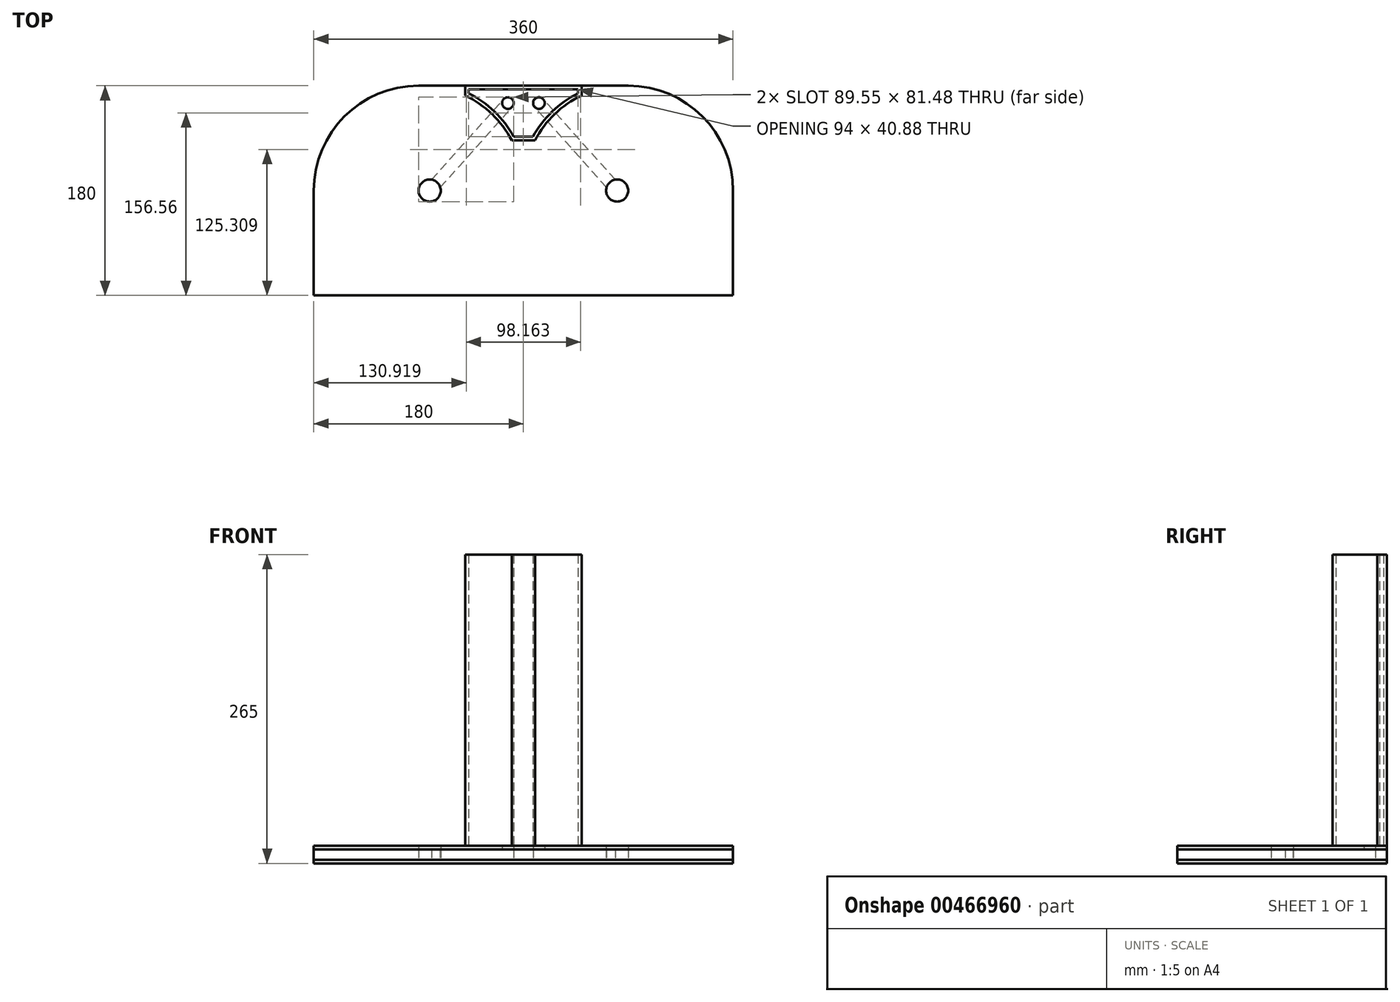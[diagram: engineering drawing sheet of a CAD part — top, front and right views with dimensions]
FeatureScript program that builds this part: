
annotation { "Feature Type Name" : "Feature", "Feature Type Description" : "" }
export const myFeature = defineFeature(function(context is Context, id is Id, definition is map)
    precondition{}
    {
        {
            var Q0;
            Q0=qCreatedBy(makeId("Top.planeOp"),FACE);
            var sketch = newSketch(context, id + "F0", { "sketchPlane" : qUnion([Q0])});
            skLineSegment(sketch, "E0.bottom", {"start": v(-180, 90) * mm, "end": v(180, 90) * mm});
            skLineSegment(sketch, "E0.top", {"start": v(-180, -90) * mm, "end": v(180, -90) * mm});
            skLineSegment(sketch, "E0.left", {"start": v(-180, 90) * mm, "end": v(-180, -90) * mm});
            skLineSegment(sketch, "E0.right", {"start": v(180, 90) * mm, "end": v(180, -90) * mm});
            skPoint(sketch, "E0.middle", {"position": v(0, 0) * mm});
            skArc(sketch, "E1", {"start": v(-78.84, 9.35) * mm, "mid": v(-86.83, -7.08) * mm, "end": v(-71.39, 2.69) * mm});
            skLineSegment(sketch, "E2", {"start": v(-80.5, 0) * mm, "end": v(0, 90) * mm, "construction": true});
            skLineSegment(sketch, "E3.0", {"start": v(-71.39, 2.69) * mm, "end": v(-9.6, 71.76) * mm});
            skLineSegment(sketch, "E4.0", {"start": v(-78.84, 9.35) * mm, "end": v(-17.06, 78.43) * mm});
            skArc(sketch, "E5", {"start": v(-9.6, 71.76) * mm, "mid": v(-10, 78.82) * mm, "end": v(-17.06, 78.43) * mm});
            skArc(sketch, "E6.MirrorCS", {"start": v(9.6, 71.76) * mm, "mid": v(10, 78.82) * mm, "end": v(17.06, 78.43) * mm});
            skLineSegment(sketch, "E7.MirrorCS", {"start": v(78.84, 9.35) * mm, "end": v(17.06, 78.43) * mm});
            skLineSegment(sketch, "E8.MirrorCS", {"start": v(71.39, 2.69) * mm, "end": v(9.6, 71.76) * mm});
            skArc(sketch, "E9.MirrorCS", {"start": v(78.84, 9.35) * mm, "mid": v(86.83, -7.08) * mm, "end": v(71.39, 2.69) * mm});
            skSolve(sketch);
        }
        {
            var Q0;
            Q0 = qSketchRegion(id + "F0", true);
            extrude(context, id + "F1", {"entities" : qUnion([Q0]), "depth" : 9 * mm});
        }
        {
            var Q0;
            Q0=makeQuery(id+"F1.opExtrude","CAP_FACE",FACE,{"disambiguationData":[OSD([sQuery(id+"F0.wireOp",EDGE,"E0.bottom"),sQuery(id+"F0.wireOp",EDGE,"E0.top"),sQuery(id+"F0.wireOp",EDGE,"E0.left"),sQuery(id+"F0.wireOp",EDGE,"E0.right"),sQuery(id+"F0.wireOp",EDGE,"E1"),sQuery(id+"F0.wireOp",EDGE,"E3.0"),sQuery(id+"F0.wireOp",EDGE,"E4.0"),sQuery(id+"F0.wireOp",EDGE,"E5"),sQuery(id+"F0.wireOp",EDGE,"E6.MirrorCS"),sQuery(id+"F0.wireOp",EDGE,"E7.MirrorCS"),sQuery(id+"F0.wireOp",EDGE,"E8.MirrorCS"),sQuery(id+"F0.wireOp",EDGE,"E9.MirrorCS")])],"isStart":false});
            var sketch = newSketch(context, id + "F2", { "sketchPlane" : qUnion([Q0])});
            skLineSegment(sketch, "E10.0", {"start": v(-180, 90) * mm, "end": v(-180, -90) * mm});
            skLineSegment(sketch, "E10.1", {"start": v(-180, 90) * mm, "end": v(180, 90) * mm});
            skLineSegment(sketch, "E10.2", {"start": v(180, 90) * mm, "end": v(180, -90) * mm});
            skLineSegment(sketch, "E10.3", {"start": v(-180, -90) * mm, "end": v(180, -90) * mm});
            skCircle(sketch, "E11", {"center": v(-80.5, 0) * mm, "radius": 9.5 * mm});
            skCircle(sketch, "E12", {"center": v(80.5, 0) * mm, "radius": 9.5 * mm});
            skCircle(sketch, "E13", {"center": v(-13.33, 75.1) * mm, "radius": 5 * mm});
            skCircle(sketch, "E14", {"center": v(13.33, 75.1) * mm, "radius": 5 * mm});
            skSolve(sketch);
        }
        {
            var Q0;
            Q0 = qSketchRegion(id + "F2", true);
            extrude(context, id + "F3", {"entities" : qUnion([Q0]), "depth" : 3 * mm});
        }
        {
            var Q0;
            Q0=makeQuery(id+"F1.opExtrude","CAP_FACE",FACE,{"disambiguationData":[OSD([sQuery(id+"F0.wireOp",EDGE,"E0.bottom"),sQuery(id+"F0.wireOp",EDGE,"E0.top"),sQuery(id+"F0.wireOp",EDGE,"E0.left"),sQuery(id+"F0.wireOp",EDGE,"E0.right"),sQuery(id+"F0.wireOp",EDGE,"E1"),sQuery(id+"F0.wireOp",EDGE,"E3.0"),sQuery(id+"F0.wireOp",EDGE,"E4.0"),sQuery(id+"F0.wireOp",EDGE,"E5"),sQuery(id+"F0.wireOp",EDGE,"E6.MirrorCS"),sQuery(id+"F0.wireOp",EDGE,"E7.MirrorCS"),sQuery(id+"F0.wireOp",EDGE,"E8.MirrorCS"),sQuery(id+"F0.wireOp",EDGE,"E9.MirrorCS")])],"isStart":true});
            var sketch = newSketch(context, id + "F4", { "sketchPlane" : qUnion([Q0])});
            skLineSegment(sketch, "E15.0", {"start": v(-180, -90) * mm, "end": v(-180, 90) * mm});
            skLineSegment(sketch, "E15.1", {"start": v(-180, 90) * mm, "end": v(180, 90) * mm});
            skCircle(sketch, "E15.2", {"center": v(-80.5, 0) * mm, "radius": 9.5 * mm, "construction": true});
            skLineSegment(sketch, "E15.3", {"start": v(-180, -90) * mm, "end": v(180, -90) * mm});
            skLineSegment(sketch, "E15.4", {"start": v(180, -90) * mm, "end": v(180, 90) * mm});
            skCircle(sketch, "E15.5", {"center": v(80.5, 0) * mm, "radius": 9.5 * mm, "construction": true});
            skSolve(sketch);
        }
        {
            var Q0;
            Q0 = qSketchRegion(id + "F4", true);
            extrude(context, id + "F5", {"entities" : qUnion([Q0]), "depth" : 3 * mm});
        }
        {
            var Q0;
            Q0=makeQuery(id+"F3.opExtrude","CAP_FACE",FACE,{"disambiguationData":[OSD([sQuery(id+"F2.wireOp",EDGE,"E10.0"),sQuery(id+"F2.wireOp",EDGE,"E10.1"),sQuery(id+"F2.wireOp",EDGE,"E10.2"),sQuery(id+"F2.wireOp",EDGE,"E10.3"),sQuery(id+"F2.wireOp",EDGE,"E11"),sQuery(id+"F2.wireOp",EDGE,"E12"),sQuery(id+"F2.wireOp",EDGE,"E13"),sQuery(id+"F2.wireOp",EDGE,"E14")])],"isStart":false});
            var sketch = newSketch(context, id + "F6", { "sketchPlane" : qUnion([Q0])});
            skLineSegment(sketch, "E16", {"start": v(-50, 90) * mm, "end": v(50, 90) * mm});
            skArc(sketch, "E17", {"start": v(-10.04, 43.12) * mm, "mid": v(-26.9, 65.58) * mm, "end": v(-50, 81.54) * mm});
            skArc(sketch, "E18", {"start": v(50, 81.57) * mm, "mid": v(26.85, 65.6) * mm, "end": v(9.96, 43.12) * mm});
            skLineSegment(sketch, "E19", {"start": v(-50, 90) * mm, "end": v(-50, 81.54) * mm});
            skLineSegment(sketch, "E20", {"start": v(50, 90) * mm, "end": v(50, 81.57) * mm});
            skLineSegment(sketch, "E21", {"start": v(-10.04, 43.12) * mm, "end": v(9.96, 43.12) * mm});
            skSolve(sketch);
        }
        {
            var Q0;
            Q0 = qSketchRegion(id + "F6", true);
            extrude(context, id + "F7", {"entities" : qUnion([Q0]), "depth" : 250 * mm});
        }
        {
            var Q0;
            Q0=makeQuery(id+"F1.opExtrude","SWEPT_EDGE",EDGE,{"disambiguationData":[OSD([sQuery(id+"F0.wireOp",EDGE,"E0.bottom"),sQuery(id+"F0.wireOp",EDGE,"E0.left")])]});
            var Q1;
            Q1=makeQuery(id+"F1.opExtrude","SWEPT_EDGE",EDGE,{"disambiguationData":[OSD([sQuery(id+"F0.wireOp",EDGE,"E0.bottom"),sQuery(id+"F0.wireOp",EDGE,"E0.right")])]});
            var Q2;
            Q2=makeQuery(id+"F3.opExtrude","SWEPT_EDGE",EDGE,{"disambiguationData":[OSD([sQuery(id+"F2.wireOp",EDGE,"E10.1"),sQuery(id+"F2.wireOp",EDGE,"E10.2")])]});
            var Q3;
            Q3=makeQuery(id+"F5.opExtrude","SWEPT_EDGE",EDGE,{"disambiguationData":[OSD([sQuery(id+"F4.wireOp",EDGE,"E15.3"),sQuery(id+"F4.wireOp",EDGE,"E15.4")])]});
            var Q4;
            Q4=makeQuery(id+"F3.opExtrude","SWEPT_EDGE",EDGE,{"disambiguationData":[OSD([sQuery(id+"F2.wireOp",EDGE,"E10.0"),sQuery(id+"F2.wireOp",EDGE,"E10.1")])]});
            var Q5;
            Q5=makeQuery(id+"F5.opExtrude","SWEPT_EDGE",EDGE,{"disambiguationData":[OSD([sQuery(id+"F4.wireOp",EDGE,"E15.0"),sQuery(id+"F4.wireOp",EDGE,"E15.3")])]});
            fillet(context, id + "F8", {"entities" : qUnion([Q0, Q1, Q2, Q3, Q4, Q5]), "radius" : 90 * mm, "tangentPropagation" : true, "allowEdgeOverflow" : false});
        }
        {
            var Q0;
            Q0=makeQuery(id+"F7.opExtrude","CAP_FACE",FACE,{"disambiguationData":[OSD([sQuery(id+"F6.wireOp",EDGE,"E16"),sQuery(id+"F6.wireOp",EDGE,"E17"),sQuery(id+"F6.wireOp",EDGE,"E18"),sQuery(id+"F6.wireOp",EDGE,"E19"),sQuery(id+"F6.wireOp",EDGE,"E20"),sQuery(id+"F6.wireOp",EDGE,"E21")])],"isStart":false});
            var Q1;
            Q1=makeQuery(id+"F7.opExtrude","CAP_FACE",FACE,{"disambiguationData":[OSD([sQuery(id+"F6.wireOp",EDGE,"E16"),sQuery(id+"F6.wireOp",EDGE,"E17"),sQuery(id+"F6.wireOp",EDGE,"E18"),sQuery(id+"F6.wireOp",EDGE,"E19"),sQuery(id+"F6.wireOp",EDGE,"E20"),sQuery(id+"F6.wireOp",EDGE,"E21")])],"isStart":true});
            shell(context, id + "F9", {"entities" : qUnion([Q0, Q1]), "thickness" : 3 * mm});
        }
    });
